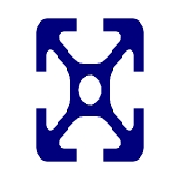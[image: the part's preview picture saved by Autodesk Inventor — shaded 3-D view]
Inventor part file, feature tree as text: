
AUTODESK INVENTOR PART (.ipt)
format: ipt  version: 2020 (Build 240168000, 168)  size: 273,920 bytes
history: native  units: mm
features: other x16, sketch x8
ambient origin geometry x8: Origin, YZ Plane, XZ Plane, XY Plane, X Axis, Y Axis, Z Axis, Center Point
bodies: Body (feature_tree)
feature tree (24):
  other  "Řízená délka"
  other  "Těleso1"
  other  "Start Plane"
  other  "End Plane"
  other  "iFeatureSketch"
  other  "DRAZKA_20:1"
  other  "DRAZKA_20:2"
  other  "DRAZKA_20:3"
  other  "DRAZKA_20:4"
  other  "DIRA_20:1"
  other  "DRAZKA_20:1Axis"
  other  "DRAZKA_20:2Axis"
  other  "DRAZKA_20:3Axis"
  other  "DRAZKA_20:4Axis"
  other  "DIRA_20:1Axis"
  sketch  "Sketch"  dims[d2=20.0mm d3=20.0mm d4=2.0mm d9=-0.0mm d10=400.0mm d11=0.13mm d12=0.0mm d15=0.83mm d16=0.83mm d17=9.8mm d18=3.0mm d19=4.55mm d20=45.0deg d21=5.2mm d22=1.8mm d24=1.0mm d26=0.83mm d27=0.83mm d28=9.8mm d29=3.0mm d30=4.55mm d31=45.0deg d32=5.2mm d33=1.8mm d35=1.0mm d37=0.83mm d38=0.83mm d39=9.8mm d40=3.0mm d41=4.55mm d42=45.0deg d43=5.2mm d44=1.8mm d46=1.0mm d48=0.83mm d49=0.83mm d50=9.8mm d51=3.0mm d52=4.55mm d53=45.0deg d54=5.2mm d55=1.8mm d57=1.0mm d59=4.3mm d60=0.0mm d61=0.0mm d62=0.0mm d63=0.0mm d64=0.0mm d65=0.0mm d66=0.0mm d67=0.0mm d76=90.0deg d14=400.0mm]
  sketch  "Náčrt11"
  other  "Pracovní rovina4"
  sketch  "Náčrt12"
  sketch  "Náčrt6"
  sketch  "Náčrt7"
  sketch  "Náčrt8"
  sketch  "Náčrt9"
  sketch  "Náčrt10"
